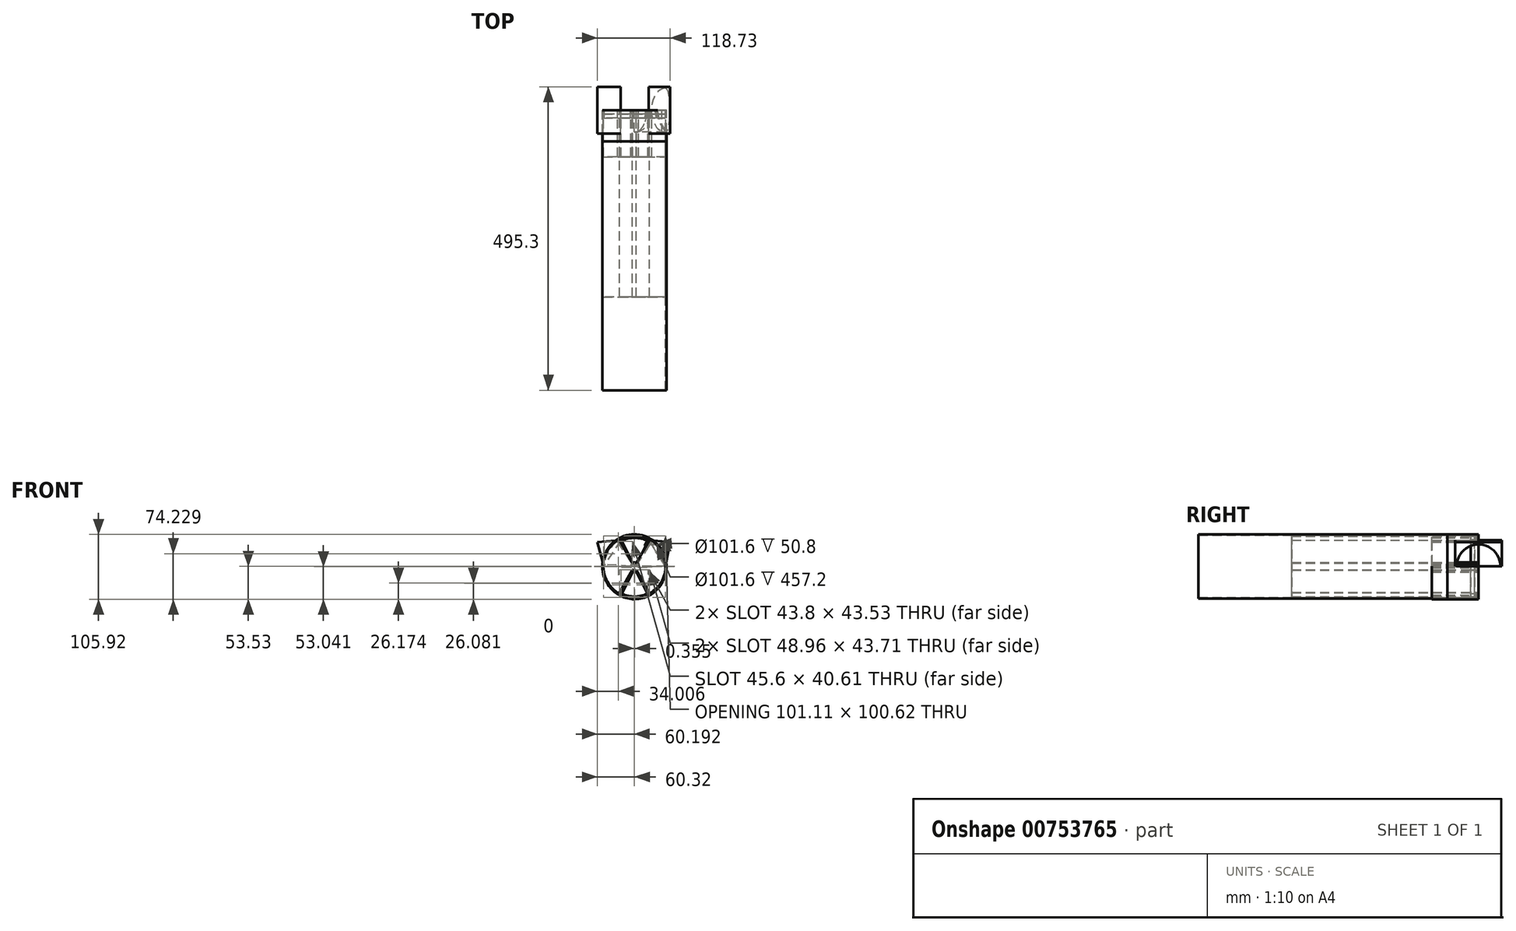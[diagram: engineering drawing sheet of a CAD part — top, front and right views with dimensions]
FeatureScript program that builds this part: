
annotation { "Feature Type Name" : "Feature", "Feature Type Description" : "" }
export const myFeature = defineFeature(function(context is Context, id is Id, definition is map)
    precondition{}
    {
        {
            var Q0;
            Q0=qCreatedBy(makeId("Front.planeOp"),FACE);
            var sketch = newSketch(context, id + "F0", { "sketchPlane" : qUnion([Q0])});
            skArc(sketch, "E0", {"start": v(-3.51, 5.3) * mm, "mid": v(-5.5, 3.17) * mm, "end": v(-6.34, 0.4) * mm});
            skCircle(sketch, "E1", {"center": v(0, 0) * mm, "radius": 50.8 * mm});
            skLineSegment(sketch, "E2", {"start": v(49.12, 3.07) * mm, "end": v(6.34, 0.4) * mm});
            skPoint(sketch, "E3.start.orphan", {"position": v(50.8, 0) * mm});
            skLineSegment(sketch, "E4.1.1", {"start": v(2.83, -5.69) * mm, "end": v(21.9, -44.07) * mm});
            skLineSegment(sketch, "E4.2.0", {"start": v(-21.9, -44.07) * mm, "end": v(-2.83, -5.69) * mm});
            skLineSegment(sketch, "E4.3.1", {"start": v(-6.34, 0.4) * mm, "end": v(-49.12, 3.07) * mm});
            skLineSegment(sketch, "E4.4.0", {"start": v(-27.22, 41) * mm, "end": v(-3.51, 5.3) * mm});
            skLineSegment(sketch, "E4.4.1", {"start": v(-2.83, 5.69) * mm, "end": v(-21.9, 44.07) * mm});
            skLineSegment(sketch, "E4.5.0", {"start": v(21.9, 44.07) * mm, "end": v(2.83, 5.69) * mm});
            skLineSegment(sketch, "E4.5.1", {"start": v(3.51, 5.3) * mm, "end": v(27.22, 41) * mm});
            skArc(sketch, "E5.trimOffspring", {"start": v(2.83, 5.69) * mm, "mid": v(0, 6.35) * mm, "end": v(-2.83, 5.69) * mm});
            skArc(sketch, "E6.trimOffspring", {"start": v(6.34, 0.4) * mm, "mid": v(5.5, 3.18) * mm, "end": v(3.51, 5.3) * mm});
            skArc(sketch, "E7.trimOffspring", {"start": v(3.51, -5.3) * mm, "mid": v(5.5, -3.17) * mm, "end": v(6.34, -0.4) * mm});
            skArc(sketch, "E8.trimOffspring", {"start": v(-2.83, -5.69) * mm, "mid": v(0, -6.35) * mm, "end": v(2.83, -5.69) * mm});
            skArc(sketch, "E9.trimOffspring", {"start": v(-6.34, -0.4) * mm, "mid": v(-5.5, -3.18) * mm, "end": v(-3.51, -5.3) * mm});
            skArc(sketch, "E10", {"start": v(-27.22, 41) * mm, "mid": v(-42.62, 24.6) * mm, "end": v(-49.12, 3.07) * mm});
            skPoint(sketch, "E11.orphan", {"position": v(-22.6, 45.5) * mm});
            skPoint(sketch, "E12.orphan", {"position": v(-28.1, 42.32) * mm});
            skPoint(sketch, "E13.orphan", {"position": v(22.6, 45.5) * mm});
            skPoint(sketch, "E14.orphan", {"position": v(28.1, 42.32) * mm});
            skArc(sketch, "E15.trimOffspring", {"start": v(21.9, 44.07) * mm, "mid": v(0, 49.21) * mm, "end": v(-21.9, 44.07) * mm});
            skPoint(sketch, "E16.orphan", {"position": v(-50.7, 3.17) * mm});
            skPoint(sketch, "E17.orphan", {"position": v(-50.7, -3.17) * mm});
            skPoint(sketch, "E18.orphan", {"position": v(-28.1, -42.32) * mm});
            skArc(sketch, "E19.trimOffspring", {"start": v(-21.9, -44.07) * mm, "mid": v(0, -49.21) * mm, "end": v(21.9, -44.07) * mm});
            skPoint(sketch, "E20.orphan", {"position": v(-22.6, -45.5) * mm});
            skPoint(sketch, "E21.orphan", {"position": v(28.1, -42.32) * mm});
            skPoint(sketch, "E22.orphan", {"position": v(22.6, -45.5) * mm});
            skPoint(sketch, "E23.orphan", {"position": v(50.7, 3.17) * mm});
            skArc(sketch, "E24.trimOffspring", {"start": v(49.12, 3.07) * mm, "mid": v(42.62, 24.6) * mm, "end": v(27.22, 41) * mm});
            skPoint(sketch, "E25.orphan", {"position": v(50.7, -3.17) * mm});
            skSolve(sketch);
        }
        {
            var Q0;
            Q0=makeQuery(id+"F0.imprint","IMPRINT",FACE,{"disambiguationData":[TD([[makeQuery(id+"F0.imprint","IMPRINT",EDGE,{"derivedFrom":sQuery(id+"F0.wireOp",EDGE,"E0")}),1.0]])]});
            extrude(context, id + "F1", {"entities" : qUnion([Q0]), "depth" : 12.7 * mm, "offsetDistance" : 25.4 * mm});
        }
        {
            var Q0;
            Q0=qCreatedBy(makeId("Front.planeOp"),FACE);
            var sketch = newSketch(context, id + "F2", { "sketchPlane" : qUnion([Q0])});
            skCircle(sketch, "E26", {"center": v(0, 0) * mm, "radius": 50.8 * mm});
            skLineSegment(sketch, "E27", {"start": v(-24.6, -42.62) * mm, "end": v(-3.14, -5.44) * mm});
            skLineSegment(sketch, "E28", {"start": v(24.35, -42.77) * mm, "end": v(3.14, -5.52) * mm});
            skArc(sketch, "E29", {"start": v(3.18, 5.5) * mm, "mid": v(0.02, 6.35) * mm, "end": v(-3.14, 5.52) * mm});
            skArc(sketch, "E30", {"start": v(-24.6, -42.62) * mm, "mid": v(-0.15, -49.21) * mm, "end": v(24.35, -42.77) * mm});
            skLineSegment(sketch, "E31.trimOffspring", {"start": v(-3.14, 5.52) * mm, "end": v(-24.35, 42.77) * mm});
            skLineSegment(sketch, "E32.trimOffspring", {"start": v(3.18, 5.5) * mm, "end": v(24.6, 42.62) * mm});
            skArc(sketch, "E33.trimOffspring", {"start": v(24.6, 42.62) * mm, "mid": v(0.15, 49.21) * mm, "end": v(-24.35, 42.77) * mm});
            skArc(sketch, "E34.trimOffspring", {"start": v(-3.18, -5.5) * mm, "mid": v(-0.02, -6.35) * mm, "end": v(3.14, -5.52) * mm});
            skSolve(sketch);
        }
        {
            var Q0;
            Q0 = qSketchRegion(id + "F2", true);
            extrude(context, id + "F3", {"entities" : qUnion([Q0]), "depth" : 304.8 * mm, "offsetDistance" : 25.4 * mm});
        }
        {
            var Q0;
            Q0=qCreatedBy(makeId("Front.planeOp"),FACE);
            var sketch = newSketch(context, id + "F4", { "sketchPlane" : qUnion([Q0])});
            skArc(sketch, "E35", {"start": v(-3.16, 2.56) * mm, "mid": v(-5.14, 0.45) * mm, "end": v(-5.98, -2.33) * mm});
            skArc(sketch, "E36", {"start": v(28.45, 39.6) * mm, "mid": v(0.36, 48.07) * mm, "end": v(-27.74, 39.6) * mm});
            skLineSegment(sketch, "E37", {"start": v(51.06, 0.44) * mm, "end": v(6.7, -2.33) * mm});
            skPoint(sketch, "E38.start.orphan", {"position": v(51.16, -2.73) * mm});
            skLineSegment(sketch, "E39.1.1", {"start": v(3.18, -8.41) * mm, "end": v(22.25, -46.8) * mm});
            skLineSegment(sketch, "E39.2.0", {"start": v(-21.54, -46.8) * mm, "end": v(-2.47, -8.41) * mm});
            skLineSegment(sketch, "E39.3.1", {"start": v(-5.98, -2.33) * mm, "end": v(-50.35, 0.44) * mm});
            skLineSegment(sketch, "E39.4.0", {"start": v(-27.74, 39.6) * mm, "end": v(-3.16, 2.56) * mm});
            skLineSegment(sketch, "E39.4.1", {"start": v(-2.47, 2.96) * mm, "end": v(-21.54, 41.35) * mm});
            skLineSegment(sketch, "E39.5.0", {"start": v(22.25, 41.35) * mm, "end": v(3.18, 2.96) * mm});
            skLineSegment(sketch, "E39.5.1", {"start": v(3.87, 2.56) * mm, "end": v(28.45, 39.6) * mm});
            skLineSegment(sketch, "E40.4.0", {"start": v(-26.86, 38.28) * mm, "end": v(-3.16, 2.56) * mm});
            skArc(sketch, "E41.trimOffspring", {"start": v(3.18, 2.96) * mm, "mid": v(0.36, 3.62) * mm, "end": v(-2.47, 2.96) * mm});
            skArc(sketch, "E42.trimOffspring", {"start": v(6.7, -2.33) * mm, "mid": v(5.85, 0.45) * mm, "end": v(3.87, 2.56) * mm});
            skArc(sketch, "E43.trimOffspring", {"start": v(3.87, -8.02) * mm, "mid": v(5.85, -5.9) * mm, "end": v(6.7, -3.12) * mm});
            skArc(sketch, "E44.trimOffspring", {"start": v(-2.47, -8.41) * mm, "mid": v(0.36, -9.08) * mm, "end": v(3.18, -8.41) * mm});
            skArc(sketch, "E45.trimOffspring", {"start": v(-5.98, -3.12) * mm, "mid": v(-5.14, -5.9) * mm, "end": v(-3.16, -8.02) * mm});
            skPoint(sketch, "E46.orphan", {"position": v(-22.25, 42.77) * mm});
            skPoint(sketch, "E47.orphan", {"position": v(-27.74, 39.6) * mm});
            skPoint(sketch, "E48.orphan", {"position": v(22.96, 42.77) * mm});
            skPoint(sketch, "E49.orphan", {"position": v(28.45, 39.6) * mm});
            skArc(sketch, "E50.trimOffspring", {"start": v(22.25, 41.35) * mm, "mid": v(0.36, 46.49) * mm, "end": v(-21.54, 41.35) * mm});
            skPoint(sketch, "E51.orphan", {"position": v(-50.35, 0.44) * mm});
            skPoint(sketch, "E52.orphan", {"position": v(-50.35, -5.9) * mm});
            skPoint(sketch, "E53.orphan", {"position": v(-27.74, -45.05) * mm});
            skArc(sketch, "E54.trimOffspring", {"start": v(-21.54, -46.8) * mm, "mid": v(0.36, -51.94) * mm, "end": v(22.25, -46.8) * mm});
            skPoint(sketch, "E55.orphan", {"position": v(-22.25, -48.22) * mm});
            skPoint(sketch, "E56.orphan", {"position": v(28.45, -45.05) * mm});
            skPoint(sketch, "E57.orphan", {"position": v(22.96, -48.22) * mm});
            skPoint(sketch, "E58.orphan", {"position": v(51.06, 0.44) * mm});
            skPoint(sketch, "E59.orphan", {"position": v(51.06, -5.9) * mm});
            skArc(sketch, "E60.trimOffspring", {"start": v(-48.76, 0.34) * mm, "mid": v(0.36, -51.94) * mm, "end": v(49.47, 0.34) * mm});
            skArc(sketch, "E61.trimOffspring", {"start": v(-50.35, 0.44) * mm, "mid": v(0.36, -53.53) * mm, "end": v(51.06, 0.44) * mm});
            skSolve(sketch);
        }
        {
            var Q0;
            {var subQ3=sQuery(id+"F4.wireOp",EDGE,"E61.trimOffspring");Q0=makeQuery(id+"F4.imprint","IMPRINT",FACE,{"disambiguationData":[TD([[makeQuery(id+"F4.imprint","IMPRINT",EDGE,{"derivedFrom":subQ3}),1.0]])]});}
            var Q1;
            {var subQ2=sQuery(id+"F4.wireOp",EDGE,"E35");Q1=makeQuery(id+"F4.imprint","IMPRINT",FACE,{"disambiguationData":[TD([[makeQuery(id+"F4.imprint","IMPRINT",EDGE,{"derivedFrom":subQ2}),1.0]])]});}
            extrude(context, id + "F5", {"entities" : qUnion([Q0, Q1]), "depth" : 76.2 * mm, "offsetDistance" : 25.4 * mm});
        }
        {
            var Q0;
            Q0=makeQuery(id+"F2.imprint","IMPRINT",FACE,{"disambiguationData":[TD([[makeQuery(id+"F2.imprint","IMPRINT",EDGE,{"derivedFrom":sQuery(id+"F2.wireOp",EDGE,"E26")}),1.0]])]});
            extrude(context, id + "F6", {"entities" : qUnion([Q0]), "depth" : 6.35 * mm, "offsetDistance" : 25.4 * mm});
        }
        {
            var Q0;
            Q0=qCreatedBy(makeId("Front.planeOp"),FACE);
            var sketch = newSketch(context, id + "F7", { "sketchPlane" : qUnion([Q0])});
            skCircle(sketch, "E62", {"center": v(0, 0) * mm, "radius": 50.8 * mm});
            skCircle(sketch, "E63", {"center": v(0, 0) * mm, "radius": 52.39 * mm});
            skSolve(sketch);
        }
        {
            var Q0;
            Q0=makeQuery(id+"F7.imprint","IMPRINT",FACE,{"disambiguationData":[TD([[makeQuery(id+"F7.imprint","IMPRINT",EDGE,{"derivedFrom":sQuery(id+"F7.wireOp",EDGE,"E62")}),-1.0]])]});
            extrude(context, id + "F8", {"entities" : qUnion([Q0]), "depth" : 457.2 * mm, "offsetDistance" : 25.4 * mm});
        }
        {
            var Q0;
            Q0=makeQuery(id+"F7.imprint","IMPRINT",FACE,{"disambiguationData":[TD([[makeQuery(id+"F7.imprint","IMPRINT",EDGE,{"derivedFrom":sQuery(id+"F7.wireOp",EDGE,"E62")}),-1.0]])]});
            extrude(context, id + "F9", {"entities" : qUnion([Q0]), "depth" : 50.8 * mm, "offsetDistance" : 25.4 * mm});
        }
        {
            var Q0;
            Q0=qCreatedBy(makeId("Front.planeOp"),FACE);
            var sketch = newSketch(context, id + "F10", { "sketchPlane" : qUnion([Q0])});
            skLineSegment(sketch, "E64", {"start": v(-60.32, 39.5) * mm, "end": v(-50.2, 0) * mm});
            skLineSegment(sketch, "E65", {"start": v(58.41, 39.5) * mm, "end": v(50.68, 0) * mm});
            skLineSegment(sketch, "E66", {"start": v(-60.32, 39.5) * mm, "end": v(-22.44, 42.67) * mm});
            skLineSegment(sketch, "E67", {"start": v(58.41, 39.5) * mm, "end": v(23.34, 42.78) * mm});
            skLineSegment(sketch, "E68", {"start": v(-22.44, 42.67) * mm, "end": v(-50.2, 0) * mm});
            skLineSegment(sketch, "E69", {"start": v(23.34, 42.78) * mm, "end": v(50.68, 0) * mm});
            skSolve(sketch);
        }
        {
            var Q0;
            Q0=makeQuery(id+"F10.imprint","IMPRINT",FACE,{"disambiguationData":[TD([[makeQuery(id+"F10.imprint","IMPRINT",EDGE,{"derivedFrom":sQuery(id+"F10.wireOp",EDGE,"E65")}),-1.0]])]});
            var Q1;
            Q1=makeQuery(id+"F10.imprint","IMPRINT",FACE,{"disambiguationData":[TD([[makeQuery(id+"F10.imprint","IMPRINT",EDGE,{"derivedFrom":sQuery(id+"F10.wireOp",EDGE,"E64")}),1.0]])]});
            extrude(context, id + "F11", {"entities" : qUnion([Q0, Q1]), "endBound" : BoundingType.SYMMETRIC, "depth" : 76.2 * mm, "offsetDistance" : 25.4 * mm});
        }
        {
            var Q0;
            Q0=qCreatedBy(makeId("Right.planeOp"),FACE);
            var sketch = newSketch(context, id + "F12", { "sketchPlane" : qUnion([Q0])});
            skArc(sketch, "E70", {"start": v(35.93, 0) * mm, "mid": v(0, 35.93) * mm, "end": v(-35.93, 0) * mm});
            skLineSegment(sketch, "E71", {"start": v(0, 0) * mm, "end": v(35.93, 0) * mm});
            skLineSegment(sketch, "E72", {"start": v(0, 0) * mm, "end": v(-35.93, 0) * mm});
            skSolve(sketch);
        }
        {
            var Q0;
            Q0=makeQuery(id+"F12.imprint","IMPRINT",FACE,{"disambiguationData":[TD([[makeQuery(id+"F12.imprint","IMPRINT",EDGE,{"derivedFrom":sQuery(id+"F12.wireOp",EDGE,"E70")}),1.0]])]});
            extrude(context, id + "F13", {"entities" : qUnion([Q0]), "operationType" : NewBodyOperationType.REMOVE, "surfaceOperationType" : NewSurfaceOperationType.ADD, "endBound" : BoundingType.THROUGH_ALL, "depth" : 76.2 * mm, "offsetDistance" : 25.4 * mm, "hasSecondDirectionDraft" : true, "secondDirectionDraftAngle" : 0 * degree});
        }
    });
